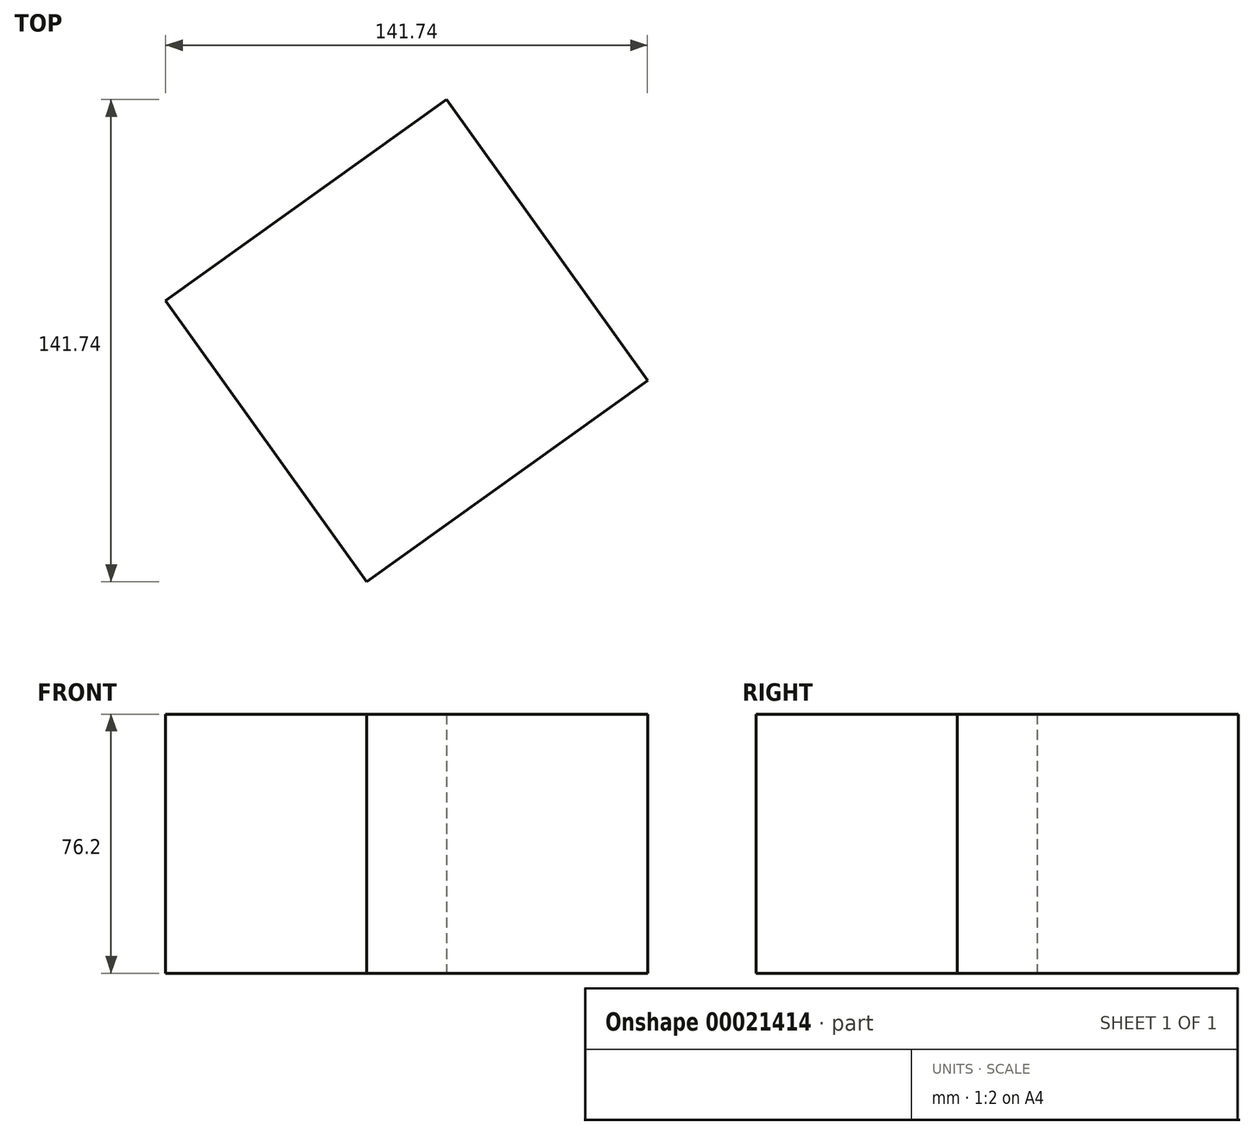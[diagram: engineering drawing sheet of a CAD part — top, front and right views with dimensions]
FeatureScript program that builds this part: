
annotation { "Feature Type Name" : "Feature", "Feature Type Description" : "" }
export const myFeature = defineFeature(function(context is Context, id is Id, definition is map)
    precondition{}
    {
        {
            var Q0;
            Q0=qCreatedBy(makeId("Top.planeOp"),FACE);
            var sketch = newSketch(context, id + "F0", { "sketchPlane" : qUnion([Q0])});
            skCircle(sketch, "E0", {"center": v(0, 0) * mm, "radius": 50.8 * mm});
            skCircle(sketch, "E1.cCircle", {"center": v(0, 0) * mm, "radius": 50.8 * mm, "construction": true});
            skLineSegment(sketch, "E1.0", {"start": v(-70.87, 11.76) * mm, "end": v(11.76, 70.87) * mm});
            skLineSegment(sketch, "E1.1", {"start": v(11.76, 70.87) * mm, "end": v(70.87, -11.76) * mm});
            skLineSegment(sketch, "E1.2", {"start": v(70.87, -11.76) * mm, "end": v(-11.76, -70.87) * mm});
            skLineSegment(sketch, "E1.3", {"start": v(-11.76, -70.87) * mm, "end": v(-70.87, 11.76) * mm});
            skPoint(sketch, "E1.0.midPoint", {"position": v(-29.56, 41.31) * mm});
            skCircle(sketch, "E2", {"center": v(0, 0) * mm, "radius": 6.35 * mm});
            skSolve(sketch);
        }
        {
            var Q0;
            Q0=makeQuery(id+"F0.imprint","IMPRINT",FACE,{"disambiguationData":[TD([[makeQuery(id+"F0.imprint","IMPRINT",EDGE,{"derivedFrom":sQuery(id+"F0.wireOp",EDGE,"E2")}),-1.0]])]});
            var Q1;
            {var subQ1=sQuery(id+"F0.wireOp",EDGE,"E0");var subQ3=sQuery(id+"F0.wireOp",EDGE,"E1.1");var subQ5=makeQuery(id+"F0.imprint","INTERSECT",VERTEX,{"derivedFrom":[subQ1,subQ3]});Q1=makeQuery(id+"F0.imprint","IMPRINT",FACE,{"disambiguationData":[TD([[makeQuery(id+"F0.imprint","IMPRINT",EDGE,{"disambiguationData":[TD([[subQ5,1.0]])],"derivedFrom":subQ1}),-1.0]])]});}
            var Q2;
            {var subQ0=sQuery(id+"F0.wireOp",EDGE,"E1.3");var subQ1=sQuery(id+"F0.wireOp",EDGE,"E0");var subQ2=makeQuery(id+"F0.imprint","INTERSECT",VERTEX,{"derivedFrom":[subQ1,subQ0]});Q2=makeQuery(id+"F0.imprint","IMPRINT",FACE,{"disambiguationData":[TD([[makeQuery(id+"F0.imprint","IMPRINT",EDGE,{"disambiguationData":[TD([[subQ2,-1.0]])],"derivedFrom":subQ1}),-1.0]])]});}
            var Q3;
            {var subQ1=sQuery(id+"F0.wireOp",EDGE,"E0");var subQ3=sQuery(id+"F0.wireOp",EDGE,"E1.0");var subQ5=makeQuery(id+"F0.imprint","INTERSECT",VERTEX,{"derivedFrom":[subQ1,subQ3]});Q3=makeQuery(id+"F0.imprint","IMPRINT",FACE,{"disambiguationData":[TD([[makeQuery(id+"F0.imprint","IMPRINT",EDGE,{"disambiguationData":[TD([[subQ5,-1.0]])],"derivedFrom":subQ1}),-1.0]])]});}
            var Q4;
            {var subQ1=sQuery(id+"F0.wireOp",EDGE,"E0");var subQ3=sQuery(id+"F0.wireOp",EDGE,"E1.0");var subQ5=makeQuery(id+"F0.imprint","INTERSECT",VERTEX,{"derivedFrom":[subQ1,subQ3]});Q4=makeQuery(id+"F0.imprint","IMPRINT",FACE,{"disambiguationData":[TD([[makeQuery(id+"F0.imprint","IMPRINT",EDGE,{"disambiguationData":[TD([[subQ5,1.0]])],"derivedFrom":subQ1}),-1.0]])]});}
            var Q5;
            Q5=makeQuery(id+"F0.imprint","IMPRINT",FACE,{"disambiguationData":[TD([[makeQuery(id+"F0.imprint","IMPRINT",EDGE,{"derivedFrom":sQuery(id+"F0.wireOp",EDGE,"E2")}),1.0]])]});
            extrude(context, id + "F1", {"entities" : qUnion([Q0, Q1, Q2, Q3, Q4, Q5]), "depth" : 76.2 * mm});
        }
        {
            var Q0;
            Q0=qCreatedBy(makeId("Top.planeOp"),FACE);
            var sketch = newSketch(context, id + "F2", { "sketchPlane" : qUnion([Q0])});
            skCircle(sketch, "E3", {"center": v(0, 0) * mm, "radius": 6.35 * mm});
            skCircle(sketch, "E4", {"center": v(0, 0) * mm, "radius": 50.8 * mm});
            skSolve(sketch);
        }
        {
            var Q0;
            Q0=makeQuery(id+"F2.imprint","IMPRINT",FACE,{"disambiguationData":[TD([[makeQuery(id+"F2.imprint","IMPRINT",EDGE,{"derivedFrom":sQuery(id+"F2.wireOp",EDGE,"E3")}),-1.0]])]});
            extrude(context, id + "F3", {"entities" : qUnion([Q0]), "operationType" : NewBodyOperationType.ADD, "depth" : 69.85 * mm});
        }
    });
